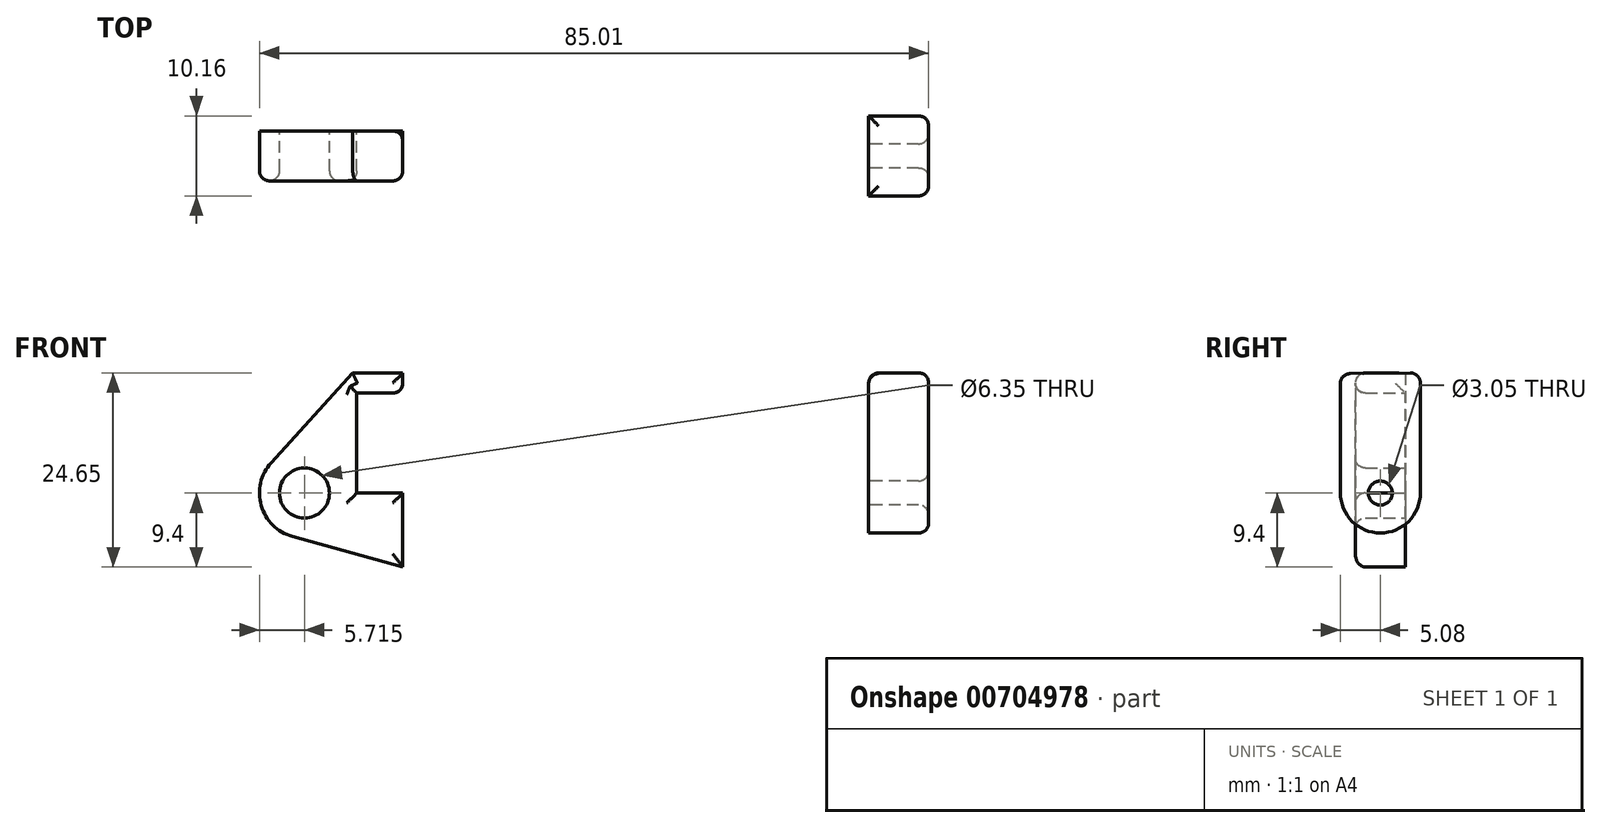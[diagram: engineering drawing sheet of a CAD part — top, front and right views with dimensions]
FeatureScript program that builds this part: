
annotation { "Feature Type Name" : "Feature", "Feature Type Description" : "" }
export const myFeature = defineFeature(function(context is Context, id is Id, definition is map)
    precondition{}
    {
        {
            var Q0;
            Q0=qCreatedBy(makeId("Front.planeOp"),FACE);
            var sketch = newSketch(context, id + "F0", { "sketchPlane" : qUnion([Q0])});
            skLineSegment(sketch, "E0", {"start": v(0, 0) * mm, "end": v(0, 12.7) * mm});
            skLineSegment(sketch, "E1", {"start": v(0, 12.7) * mm, "end": v(10.16, 12.7) * mm});
            skLineSegment(sketch, "E2", {"start": v(10.16, 12.7) * mm, "end": v(10.16, 10.16) * mm});
            skLineSegment(sketch, "E3", {"start": v(10.16, 10.16) * mm, "end": v(56.13, 10.16) * mm});
            skLineSegment(sketch, "E4", {"start": v(56.13, 10.16) * mm, "end": v(56.13, 12.7) * mm});
            skLineSegment(sketch, "E5", {"start": v(56.13, 12.7) * mm, "end": v(66.3, 12.7) * mm});
            skLineSegment(sketch, "E6", {"start": v(66.3, 12.7) * mm, "end": v(66.3, 0) * mm});
            skLineSegment(sketch, "E7", {"start": v(66.3, 0) * mm, "end": v(0, 0) * mm});
            skLineSegment(sketch, "E8", {"start": v(5.84, 15.24) * mm, "end": v(-0.5, 15.24) * mm});
            skLineSegment(sketch, "E9", {"start": v(-0.5, 15.24) * mm, "end": v(-10.88, 3.85) * mm});
            skLineSegment(sketch, "E10", {"start": v(0, 0) * mm, "end": v(-6.65, 0) * mm});
            skCircle(sketch, "E11", {"center": v(-6.65, 0) * mm, "radius": 5.72 * mm});
            skCircle(sketch, "E12", {"center": v(-6.65, 0) * mm, "radius": 3.18 * mm});
            skLineSegment(sketch, "E13", {"start": v(5.84, 15.24) * mm, "end": v(5.84, -9.4) * mm});
            skLineSegment(sketch, "E14", {"start": v(5.84, -9.4) * mm, "end": v(-8.18, -5.5) * mm});
            skSolve(sketch);
        }
        {
            var Q0;
            {var subQ0=sQuery(id+"F0.wireOp",EDGE,"E2");Q0=makeQuery(id+"F0.imprint","IMPRINT",FACE,{"disambiguationData":[TD([[makeQuery(id+"F0.imprint","IMPRINT",EDGE,{"derivedFrom":subQ0}),-1.0]])]});}
            var Q1;
            Q1=sQuery(id+"F0.wireOp",EDGE,"E2");
            var Q2;
            Q2=sQuery(id+"F0.wireOp",EDGE,"E1");
            var Q3;
            Q3=sQuery(id+"F0.wireOp",EDGE,"E0");
            var Q4;
            Q4=sQuery(id+"F0.wireOp",EDGE,"E7");
            revolve(context, id + "F1", {"bodyType" : ToolBodyType.SURFACE, "entities" : qUnion([Q0]), "surfaceEntities" : qUnion([Q1, Q2, Q3]), "axis" : qUnion([Q4]), "revolveType" : RevolveType.FULL});
        }
        {
            var Q0;
            Q0=sQuery(id+"F0.wireOp",EDGE,"E3");
            var Q1;
            Q1=sQuery(id+"F0.wireOp",EDGE,"E4");
            var Q2;
            Q2=sQuery(id+"F0.wireOp",EDGE,"E5");
            var Q3;
            Q3=sQuery(id+"F0.wireOp",EDGE,"E6");
            var Q4;
            Q4=sQuery(id+"F0.wireOp",EDGE,"E7");
            revolve(context, id + "F2", {"bodyType" : ToolBodyType.SURFACE, "surfaceEntities" : qUnion([Q0, Q1, Q2, Q3]), "axis" : qUnion([Q4]), "revolveType" : RevolveType.FULL});
        }
        {
            var Q0;
            {var subQ5=sQuery(id+"F0.wireOp",EDGE,"E12");Q0=makeQuery(id+"F0.imprint","IMPRINT",FACE,{"disambiguationData":[TD([[makeQuery(id+"F0.imprint","IMPRINT",EDGE,{"derivedFrom":subQ5}),-1.0]])]});}
            var Q1;
            {var subQ1=sQuery(id+"F0.wireOp",EDGE,"E0");Q1=makeQuery(id+"F0.imprint","IMPRINT",FACE,{"disambiguationData":[TD([[makeQuery(id+"F0.imprint","IMPRINT",EDGE,{"derivedFrom":subQ1}),1.0]])]});}
            var Q2;
            {var subQ0=sQuery(id+"F0.wireOp",EDGE,"E14");Q2=makeQuery(id+"F0.imprint","IMPRINT",FACE,{"disambiguationData":[TD([[makeQuery(id+"F0.imprint","IMPRINT",EDGE,{"derivedFrom":subQ0}),-1.0]])]});}
            extrude(context, id + "F3", {"entities" : qUnion([Q0, Q1, Q2]), "endBound" : BoundingType.SYMMETRIC, "depth" : 6.35 * mm, "offsetDistance" : 25.4 * mm});
        }
        {
            var Q0;
            Q0=makeQuery(id+"F2.opRevolve","SWEPT_FACE",FACE,{"disambiguationData":[OSD([sQuery(id+"F0.wireOp",EDGE,"E6")])]});
            var sketch = newSketch(context, id + "F4", { "sketchPlane" : qUnion([Q0])});
            skCircle(sketch, "E15", {"center": v(0, 0) * mm, "radius": 5.08 * mm});
            skCircle(sketch, "E16", {"center": v(0, 0) * mm, "radius": 1.52 * mm});
            skLineSegment(sketch, "E17", {"start": v(-5.08, 0) * mm, "end": v(-5.08, 15.16) * mm});
            skLineSegment(sketch, "E18", {"start": v(5.08, 0) * mm, "end": v(5.08, 15.27) * mm});
            skLineSegment(sketch, "E19", {"start": v(5.08, 15.27) * mm, "end": v(-5.08, 15.16) * mm});
            skSolve(sketch);
        }
        {
            var Q0;
            Q0 = qSketchRegion(id + "F4", true);
            extrude(context, id + "F5", {"entities" : qUnion([Q0]), "depth" : 6.35 * mm, "offsetDistance" : 25.4 * mm, "hasSecondDirection" : true, "secondDirectionOppositeDirection" : true, "secondDirectionDepth" : 1.27 * mm});
        }
        {
            var Q0;
            Q0=makeQuery(id+"F3.opExtrude","SWEPT_FACE",FACE,{"disambiguationData":[OSD([sQuery(id+"F0.wireOp",EDGE,"E8")])]});
            var sketch = newSketch(context, id + "F6", { "sketchPlane" : qUnion([Q0])});
            skCircle(sketch, "E20", {"center": v(2.67, -0.05) * mm, "radius": 1.52 * mm});
            skPoint(sketch, "E20.centerSnap0", {"position": v(2.67, 3.18) * mm});
            skCircle(sketch, "E21", {"center": v(68.74, 0.14) * mm, "radius": 1.52 * mm});
            skSolve(sketch);
        }
        {
            var Q0;
            Q0=sQuery(id+"F6.wireOp",EDGE,"E20");
            extrude(context, id + "F7", {"bodyType" : ToolBodyType.SURFACE, "surfaceEntities" : qUnion([Q0]), "oppositeDirection" : true, "depth" : 17.78 * mm, "offsetDistance" : 25.4 * mm});
        }
        {
            var Q0;
            Q0=makeQuery(id+"F5.opExtrude","SWEPT_FACE",FACE,{"disambiguationData":[OSD([sQuery(id+"F4.wireOp",EDGE,"E19")])]});
            var sketch = newSketch(context, id + "F8", { "sketchPlane" : qUnion([Q0])});
            skCircle(sketch, "E22", {"center": v(69.5, 0.15) * mm, "radius": 1.52 * mm});
            skPoint(sketch, "E22.centerSnap0", {"position": v(65.02, 0.15) * mm});
            skSolve(sketch);
        }
        {
            var Q0;
            Q0 = qSketchRegion(id + "F8", true);
            extrude(context, id + "F9", {"entities" : qUnion([Q0]), "operationType" : NewBodyOperationType.ADD, "oppositeDirection" : true, "depth" : 10.4 * mm, "offsetDistance" : 25.4 * mm});
        }
        {
            var Q0;
            Q0=makeQuery(id+"F1.opRevolve","SWEPT_EDGE",EDGE,{"disambiguationData":[OSD([sQuery(id+"F0.wireOp",VERTEX,"E1.end")])]});
            var Q1;
            Q1=makeQuery(id+"F2.opRevolve","SWEPT_FACE",FACE,{"disambiguationData":[OSD([sQuery(id+"F0.wireOp",EDGE,"E3")])]});
            var Q2;
            Q2=makeQuery(id+"F3.opExtrude","CAP_EDGE",EDGE,{"disambiguationData":[OSD([sQuery(id+"F0.wireOp",EDGE,"E8")])],"isStart":false});
            var Q3;
            {var subQ0=sQuery(id+"F0.wireOp",EDGE,"E13");Q3=makeQuery(id+"F3.opExtrude","CAP_EDGE",EDGE,{"disambiguationData":[OSD([subQ0]),TDD([makeQuery(id+"F0.imprint","IMPRINT",EDGE,{"disambiguationData":[TD([[makeQuery(id+"F0.imprint","INTERSECT",VERTEX,{"derivedFrom":[sQuery(id+"F0.wireOp",EDGE,"E8"),subQ0]}),-1.0]])],"derivedFrom":subQ0})])],"isStart":true});}
            var Q4;
            Q4=makeQuery(id+"F3.opExtrude","SWEPT_EDGE",EDGE,{"disambiguationData":[OSD([sQuery(id+"F0.wireOp",EDGE,"E1"),sQuery(id+"F0.wireOp",EDGE,"E13")])]});
            var Q5;
            Q5=makeQuery(id+"F3.opExtrude","CAP_EDGE",EDGE,{"disambiguationData":[OSD([sQuery(id+"F0.wireOp",EDGE,"E9")])],"isStart":false});
            var Q6;
            Q6=makeQuery(id+"F3.opExtrude","CAP_EDGE",EDGE,{"disambiguationData":[OSD([sQuery(id+"F0.wireOp",EDGE,"E11")])],"isStart":false});
            var Q7;
            Q7=makeQuery(id+"F1.opRevolve","SWEPT_EDGE",EDGE,{"disambiguationData":[OSD([sQuery(id+"F0.wireOp",VERTEX,"E0.end")])]});
            var Q8;
            Q8=makeQuery(id+"F3.opExtrude","CAP_FACE",FACE,{"disambiguationData":[OSD([sQuery(id+"F0.wireOp",EDGE,"E0"),sQuery(id+"F0.wireOp",EDGE,"E1"),sQuery(id+"F0.wireOp",EDGE,"E7"),sQuery(id+"F0.wireOp",EDGE,"E8"),sQuery(id+"F0.wireOp",EDGE,"E9"),sQuery(id+"F0.wireOp",EDGE,"E11"),sQuery(id+"F0.wireOp",EDGE,"E12"),sQuery(id+"F0.wireOp",EDGE,"E13"),sQuery(id+"F0.wireOp",EDGE,"E14")])],"isStart":false});
            var Q9;
            Q9=makeQuery(id+"F5.opExtrude","SWEPT_EDGE",EDGE,{"disambiguationData":[OSD([sQuery(id+"F4.wireOp",EDGE,"E18"),sQuery(id+"F4.wireOp",EDGE,"E19")])]});
            var Q10;
            Q10=makeQuery(id+"F5.opExtrude","CAP_FACE",FACE,{"disambiguationData":[OSD([sQuery(id+"F4.wireOp",EDGE,"E15"),sQuery(id+"F4.wireOp",EDGE,"E16"),sQuery(id+"F4.wireOp",EDGE,"E17"),sQuery(id+"F4.wireOp",EDGE,"E18"),sQuery(id+"F4.wireOp",EDGE,"E19")])],"isStart":false});
            var Q11;
            Q11=makeQuery(id+"F5.opExtrude","SWEPT_EDGE",EDGE,{"disambiguationData":[OSD([sQuery(id+"F4.wireOp",EDGE,"E17"),sQuery(id+"F4.wireOp",EDGE,"E19")])]});
            var Q12;
            Q12=makeQuery(id+"F5.opExtrude","CAP_EDGE",EDGE,{"disambiguationData":[OSD([sQuery(id+"F4.wireOp",EDGE,"E19")])],"isStart":true});
            var Q13;
            Q13=makeQuery(id+"F2.opRevolve","SWEPT_EDGE",EDGE,{"disambiguationData":[OSD([sQuery(id+"F0.wireOp",VERTEX,"E5.start")])]});
            var Q14;
            Q14=makeQuery(id+"F2.opRevolve","SWEPT_FACE",FACE,{"disambiguationData":[OSD([sQuery(id+"F0.wireOp",EDGE,"E6")])]});
            fillet(context, id + "F10", {"entities" : qUnion([Q0, Q1, Q2, Q3, Q4, Q5, Q6, Q7, Q8, Q9, Q10, Q11, Q12, Q13, Q14]), "radius" : 1.27 * mm, "tangentPropagation" : true, "allowEdgeOverflow" : false});
        }
    });
